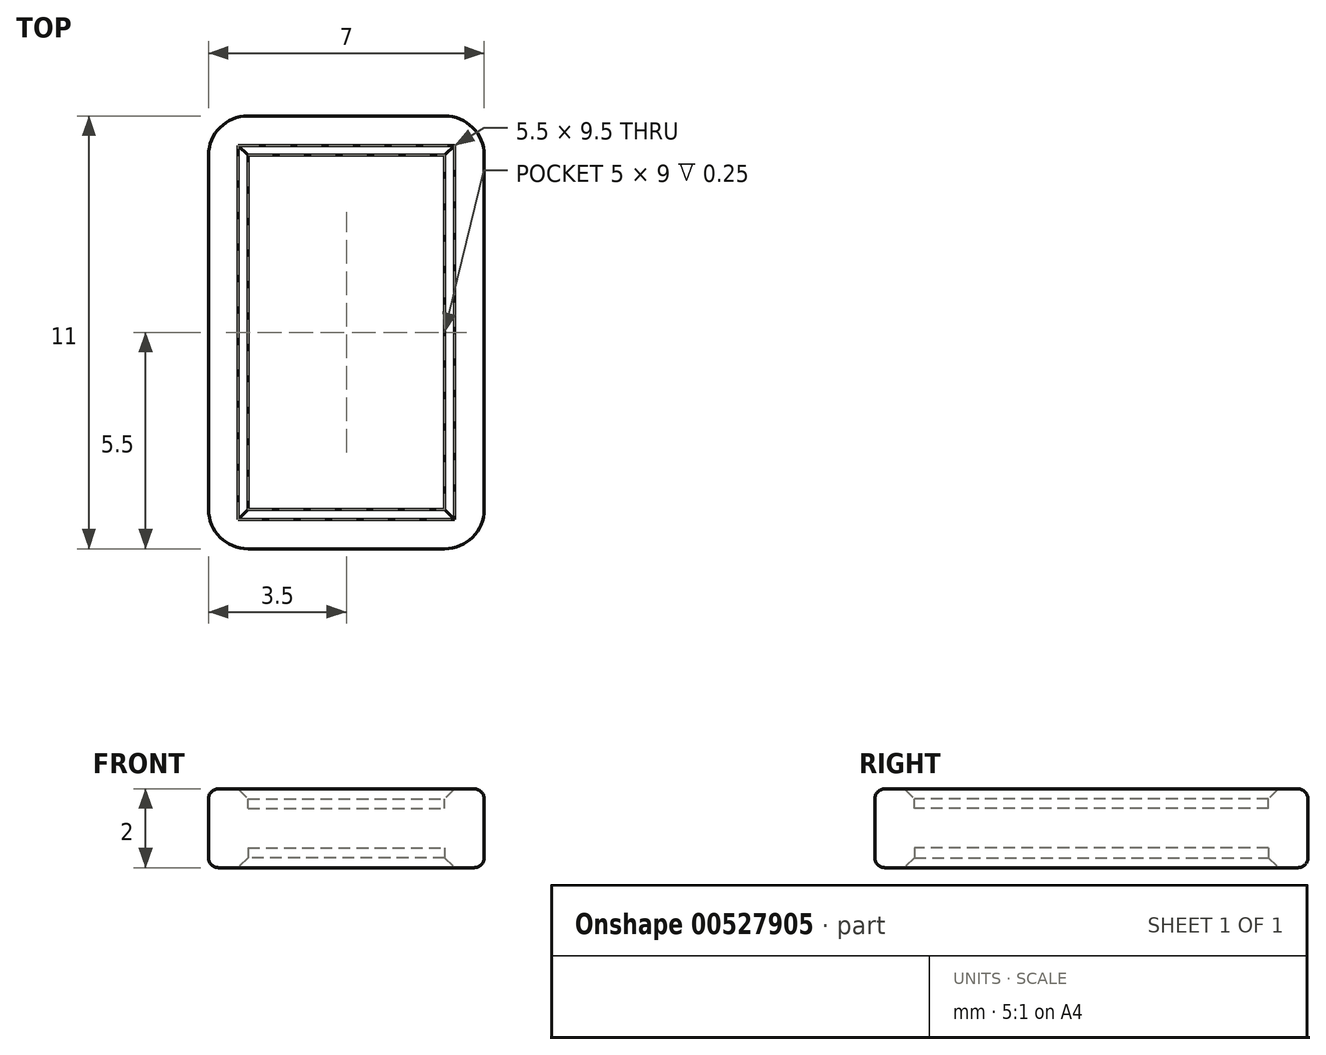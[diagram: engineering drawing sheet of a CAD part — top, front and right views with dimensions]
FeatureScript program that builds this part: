
annotation { "Feature Type Name" : "Feature", "Feature Type Description" : "" }
export const myFeature = defineFeature(function(context is Context, id is Id, definition is map)
    precondition{}
    {
        {
            var Q0;
            Q0=qCreatedBy(makeId("Top.planeOp"),FACE);
            var sketch = newSketch(context, id + "F0", { "sketchPlane" : qUnion([Q0])});
            skLineSegment(sketch, "E0.bottom", {"start": v(0, 0) * mm, "end": v(6, 0) * mm});
            skLineSegment(sketch, "E0.top", {"start": v(0, 10) * mm, "end": v(6, 10) * mm});
            skLineSegment(sketch, "E0.left", {"start": v(0, 0) * mm, "end": v(0, 10) * mm});
            skLineSegment(sketch, "E0.right", {"start": v(6, 0) * mm, "end": v(6, 10) * mm});
            skSolve(sketch);
        }
        {
            var Q0;
            Q0=makeQuery(id+"F0.imprint","IMPRINT",FACE,{"disambiguationData":[TD([[makeQuery(id+"F0.imprint","IMPRINT",EDGE,{"derivedFrom":sQuery(id+"F0.wireOp",EDGE,"E0.bottom")}),1.0]])]});
            extrude(context, id + "F1", {"entities" : qUnion([Q0]), "depth" : 1 * mm});
        }
        {
            var Q0;
            Q0=makeQuery(id+"F1.opExtrude","SWEPT_EDGE",EDGE,{"disambiguationData":[OSD([sQuery(id+"F0.wireOp",EDGE,"E0.bottom"),sQuery(id+"F0.wireOp",EDGE,"E0.right")])]});
            var Q1;
            Q1=makeQuery(id+"F1.opExtrude","SWEPT_EDGE",EDGE,{"disambiguationData":[OSD([sQuery(id+"F0.wireOp",EDGE,"E0.top"),sQuery(id+"F0.wireOp",EDGE,"E0.right")])]});
            var Q2;
            Q2=makeQuery(id+"F1.opExtrude","SWEPT_EDGE",EDGE,{"disambiguationData":[OSD([sQuery(id+"F0.wireOp",EDGE,"E0.bottom"),sQuery(id+"F0.wireOp",EDGE,"E0.left")])]});
            var Q3;
            Q3=makeQuery(id+"F1.opExtrude","SWEPT_EDGE",EDGE,{"disambiguationData":[OSD([sQuery(id+"F0.wireOp",EDGE,"E0.top"),sQuery(id+"F0.wireOp",EDGE,"E0.left")])]});
            fillet(context, id + "F2", {"entities" : qUnion([Q0, Q1, Q2, Q3]), "radius" : .5 * mm, "tangentPropagation" : true, "allowEdgeOverflow" : false});
        }
        {
            var Q0;
            Q0=qCreatedBy(makeId("Front.planeOp"),FACE);
            cPlane(context, id + "F3", {"entities" : qUnion([Q0]), "cplaneType" : CPlaneType.OFFSET, "offset" : .5 * mm, "oppositeDirection" : true, "width" : 150 * mm, "height" : 150 * mm});
        }
        {
            var Q0;
            Q0=qCreatedBy(id+"F3.planeOp",FACE);
            var sketch = newSketch(context, id + "F4", { "sketchPlane" : qUnion([Q0])});
            skLineSegment(sketch, "E1.0", {"start": v(6, 0) * mm, "end": v(5.5, 0) * mm});
            skLineSegment(sketch, "E1.1", {"start": v(6, 1) * mm, "end": v(6, 0) * mm});
            skLineSegment(sketch, "E1.2", {"start": v(5.5, 1) * mm, "end": v(6, 1) * mm});
            skLineSegment(sketch, "E2.0", {"start": v(6.5, -0.5) * mm, "end": v(5.5, -0.5) * mm});
            skLineSegment(sketch, "E2.1", {"start": v(6.5, 1.5) * mm, "end": v(6.5, -0.5) * mm});
            skLineSegment(sketch, "E2.2", {"start": v(5.5, 1.5) * mm, "end": v(6.5, 1.5) * mm});
            skLineSegment(sketch, "E3", {"start": v(5.5, 0) * mm, "end": v(5.5, -0.5) * mm});
            skLineSegment(sketch, "E4", {"start": v(5.5, 1) * mm, "end": v(5.5, 1.5) * mm});
            skSolve(sketch);
        }
        {
            var Q0;
            Q0=makeQuery(id+"F1.opExtrude","CAP_FACE",FACE,{"disambiguationData":[OSD([sQuery(id+"F0.wireOp",EDGE,"E0.bottom"),sQuery(id+"F0.wireOp",EDGE,"E0.top"),sQuery(id+"F0.wireOp",EDGE,"E0.left"),sQuery(id+"F0.wireOp",EDGE,"E0.right")])],"isStart":false});
            var sketch = newSketch(context, id + "F5", { "sketchPlane" : qUnion([Q0])});
            skLineSegment(sketch, "E5.0", {"start": v(6, 0.5) * mm, "end": v(6, 9.5) * mm});
            skArc(sketch, "E5.1", {"start": v(5.5, 0) * mm, "mid": v(5.85, 0.15) * mm, "end": v(6, 0.5) * mm});
            skLineSegment(sketch, "E5.2", {"start": v(0.5, 0) * mm, "end": v(5.5, 0) * mm});
            skArc(sketch, "E5.3", {"start": v(0, 0.5) * mm, "mid": v(0.15, 0.15) * mm, "end": v(0.5, 0) * mm});
            skLineSegment(sketch, "E5.4", {"start": v(0, 0.5) * mm, "end": v(0, 9.5) * mm});
            skArc(sketch, "E5.5", {"start": v(0.5, 10) * mm, "mid": v(0.15, 9.85) * mm, "end": v(0, 9.5) * mm});
            skLineSegment(sketch, "E5.6", {"start": v(0.5, 10) * mm, "end": v(5.5, 10) * mm});
            skArc(sketch, "E5.7", {"start": v(6, 9.5) * mm, "mid": v(5.85, 9.85) * mm, "end": v(5.5, 10) * mm});
            skSolve(sketch);
        }
        {
            var Q0;
            Q0=qSketchRegion(id+"F4",true);
            var Q1;
            Q1=sQuery(id+"F5.wireOp",EDGE,"E5.1");
            var Q2;
            Q2=sQuery(id+"F5.wireOp",EDGE,"E5.2");
            var Q3;
            Q3=sQuery(id+"F5.wireOp",EDGE,"E5.3");
            var Q4;
            Q4=sQuery(id+"F5.wireOp",EDGE,"E5.4");
            var Q5;
            Q5=sQuery(id+"F5.wireOp",EDGE,"E5.5");
            var Q6;
            Q6=sQuery(id+"F5.wireOp",EDGE,"E5.6");
            var Q7;
            Q7=sQuery(id+"F5.wireOp",EDGE,"E5.7");
            var Q8;
            Q8=sQuery(id+"F5.wireOp",EDGE,"E5.0");
            sweep(context, id + "F6", {"operationType" : NewBodyOperationType.ADD, "profiles" : qUnion([Q0]), "path" : qUnion([Q1, Q2, Q3, Q4, Q5, Q6, Q7, Q8])});
        }
        {
            var Q0;
            Q0=makeQuery(id+"F6.opSweep","SWEPT_EDGE",EDGE,{"disambiguationData":[OSD([sQuery(id+"F4.wireOp",EDGE,"E2.1"),sQuery(id+"F4.wireOp",EDGE,"E2.2"),sQuery(id+"F5.wireOp",EDGE,"E5.4")])]});
            var Q1;
            Q1=makeQuery(id+"F6.opSweep","SWEPT_EDGE",EDGE,{"disambiguationData":[OSD([sQuery(id+"F4.wireOp",EDGE,"E2.0"),sQuery(id+"F4.wireOp",EDGE,"E2.1"),sQuery(id+"F5.wireOp",EDGE,"E5.2")])]});
            fillet(context, id + "F7", {"entities" : qUnion([Q0, Q1]), "radius" : .25 * mm, "tangentPropagation" : true, "allowEdgeOverflow" : false});
        }
        {
            var Q0;
            Q0=makeQuery(id+"F6.opSweep","SWEPT_EDGE",EDGE,{"disambiguationData":[OSD([sQuery(id+"F4.wireOp",EDGE,"E2.2"),sQuery(id+"F4.wireOp",EDGE,"E4"),sQuery(id+"F5.wireOp",EDGE,"E5.4")])]});
            var Q1;
            Q1=makeQuery(id+"F6.opSweep","SWEPT_EDGE",EDGE,{"disambiguationData":[OSD([sQuery(id+"F4.wireOp",EDGE,"E2.2"),sQuery(id+"F4.wireOp",EDGE,"E4"),sQuery(id+"F5.wireOp",EDGE,"E5.6")])]});
            var Q2;
            Q2=makeQuery(id+"F6.opSweep","SWEPT_EDGE",EDGE,{"disambiguationData":[OSD([sQuery(id+"F4.wireOp",EDGE,"E2.2"),sQuery(id+"F4.wireOp",EDGE,"E4"),sQuery(id+"F5.wireOp",EDGE,"E5.0")])]});
            var Q3;
            Q3=makeQuery(id+"F6.opSweep","SWEPT_EDGE",EDGE,{"disambiguationData":[OSD([sQuery(id+"F4.wireOp",EDGE,"E2.2"),sQuery(id+"F4.wireOp",EDGE,"E4"),sQuery(id+"F5.wireOp",EDGE,"E5.2")])]});
            var Q4;
            Q4=makeQuery(id+"F6.opSweep","SWEPT_EDGE",EDGE,{"disambiguationData":[OSD([sQuery(id+"F4.wireOp",EDGE,"E2.0"),sQuery(id+"F4.wireOp",EDGE,"E3"),sQuery(id+"F5.wireOp",EDGE,"E5.4")])]});
            var Q5;
            Q5=makeQuery(id+"F6.opSweep","SWEPT_EDGE",EDGE,{"disambiguationData":[OSD([sQuery(id+"F4.wireOp",EDGE,"E2.0"),sQuery(id+"F4.wireOp",EDGE,"E3"),sQuery(id+"F5.wireOp",EDGE,"E5.2")])]});
            var Q6;
            Q6=makeQuery(id+"F6.opSweep","SWEPT_EDGE",EDGE,{"disambiguationData":[OSD([sQuery(id+"F4.wireOp",EDGE,"E2.0"),sQuery(id+"F4.wireOp",EDGE,"E3"),sQuery(id+"F5.wireOp",EDGE,"E5.0")])]});
            var Q7;
            Q7=makeQuery(id+"F6.opSweep","SWEPT_EDGE",EDGE,{"disambiguationData":[OSD([sQuery(id+"F4.wireOp",EDGE,"E2.0"),sQuery(id+"F4.wireOp",EDGE,"E3"),sQuery(id+"F5.wireOp",EDGE,"E5.6")])]});
            chamfer(context, id + "F8", {"entities" : qUnion([Q0, Q1, Q2, Q3, Q4, Q5, Q6, Q7]), "width" : .25 * mm, "tangentPropagation" : true});
        }
    });
